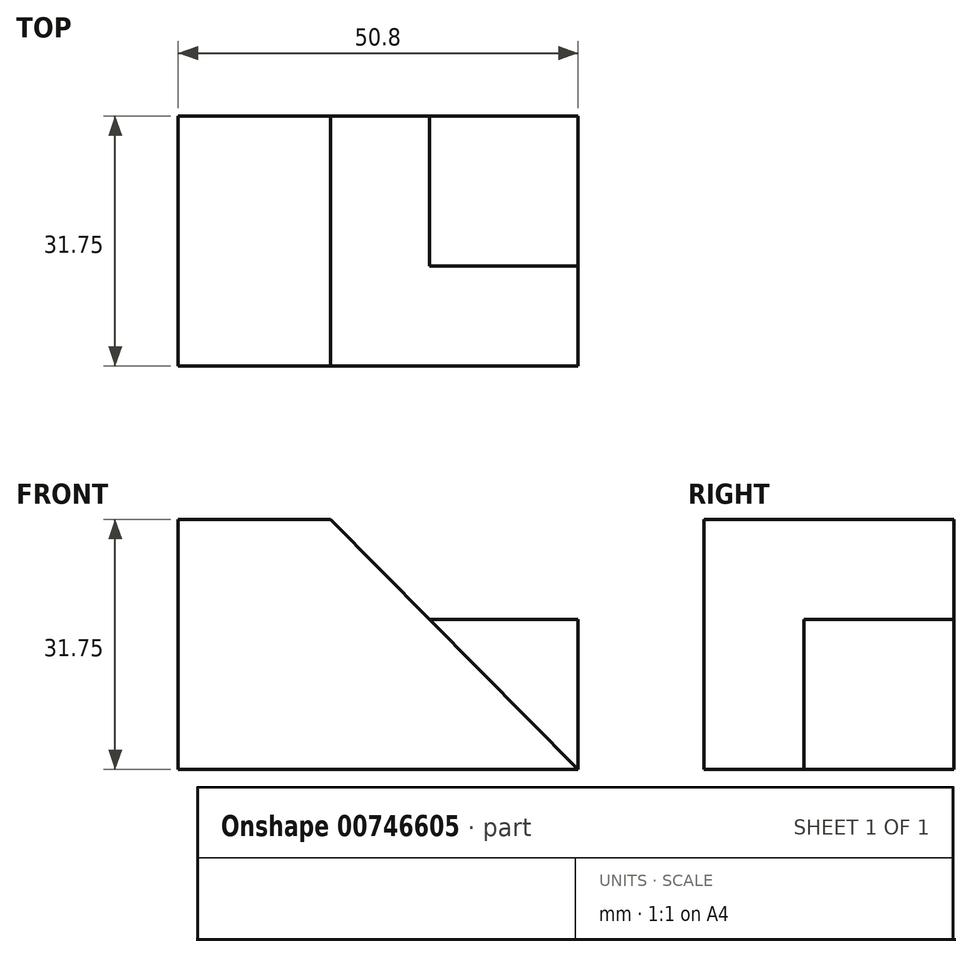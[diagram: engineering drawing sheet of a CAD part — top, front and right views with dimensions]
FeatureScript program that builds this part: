
annotation { "Feature Type Name" : "Feature", "Feature Type Description" : "" }
export const myFeature = defineFeature(function(context is Context, id is Id, definition is map)
    precondition{}
    {
        {
            var Q0;
            Q0=qCreatedBy(makeId("Front.planeOp"),FACE);
            var sketch = newSketch(context, id + "F0", { "sketchPlane" : qUnion([Q0])});
            skLineSegment(sketch, "E0.bottom", {"start": v(0, 0) * mm, "end": v(-50.8, 0) * mm});
            skLineSegment(sketch, "E0.top", {"start": v(0, 31.75) * mm, "end": v(-50.8, 31.75) * mm});
            skLineSegment(sketch, "E0.left", {"start": v(0, 0) * mm, "end": v(0, 31.75) * mm});
            skLineSegment(sketch, "E0.right", {"start": v(-50.8, 0) * mm, "end": v(-50.8, 31.75) * mm});
            skSolve(sketch);
        }
        {
            var Q0;
            Q0=makeQuery(id+"F0.imprint","IMPRINT",FACE,{"disambiguationData":[TD([[makeQuery(id+"F0.imprint","IMPRINT",EDGE,{"derivedFrom":sQuery(id+"F0.wireOp",EDGE,"E0.bottom")}),-1.0]])]});
            extrude(context, id + "F1", {"entities" : qUnion([Q0]), "depth" : 31.75 * mm, "offsetDistance" : 25.4 * mm});
        }
        {
            var Q0;
            Q0=qCreatedBy(makeId("Front.planeOp"),FACE);
            var sketch = newSketch(context, id + "F2", { "sketchPlane" : qUnion([Q0])});
            skLineSegment(sketch, "E1", {"start": v(-31.64, 31.92) * mm, "end": v(0, 0) * mm});
            skLineSegment(sketch, "E2", {"start": v(0, 0) * mm, "end": v(0, 32.2) * mm});
            skLineSegment(sketch, "E3", {"start": v(0, 32.2) * mm, "end": v(-31.64, 31.92) * mm});
            skSolve(sketch);
        }
        {
            var Q0;
            Q0 = qSketchRegion(id + "F2", true);
            extrude(context, id + "F3", {"entities" : qUnion([Q0]), "operationType" : NewBodyOperationType.REMOVE, "depth" : 38.1 * mm, "offsetDistance" : 25.4 * mm});
        }
        {
            var Q0;
            Q0=qCreatedBy(makeId("Front.planeOp"),FACE);
            var sketch = newSketch(context, id + "F4", { "sketchPlane" : qUnion([Q0])});
            skLineSegment(sketch, "E4", {"start": v(0, 0) * mm, "end": v(0, 19.05) * mm});
            skLineSegment(sketch, "E5", {"start": v(0, 19.05) * mm, "end": v(-19.05, 19.05) * mm});
            skLineSegment(sketch, "E6", {"start": v(-19.05, 19.05) * mm, "end": v(0, 0) * mm});
            skSolve(sketch);
        }
        {
            var Q0;
            Q0 = qSketchRegion(id + "F4", true);
            extrude(context, id + "F5", {"entities" : qUnion([Q0]), "operationType" : NewBodyOperationType.ADD, "depth" : 19.05 * mm, "offsetDistance" : 25.4 * mm});
        }
    });
